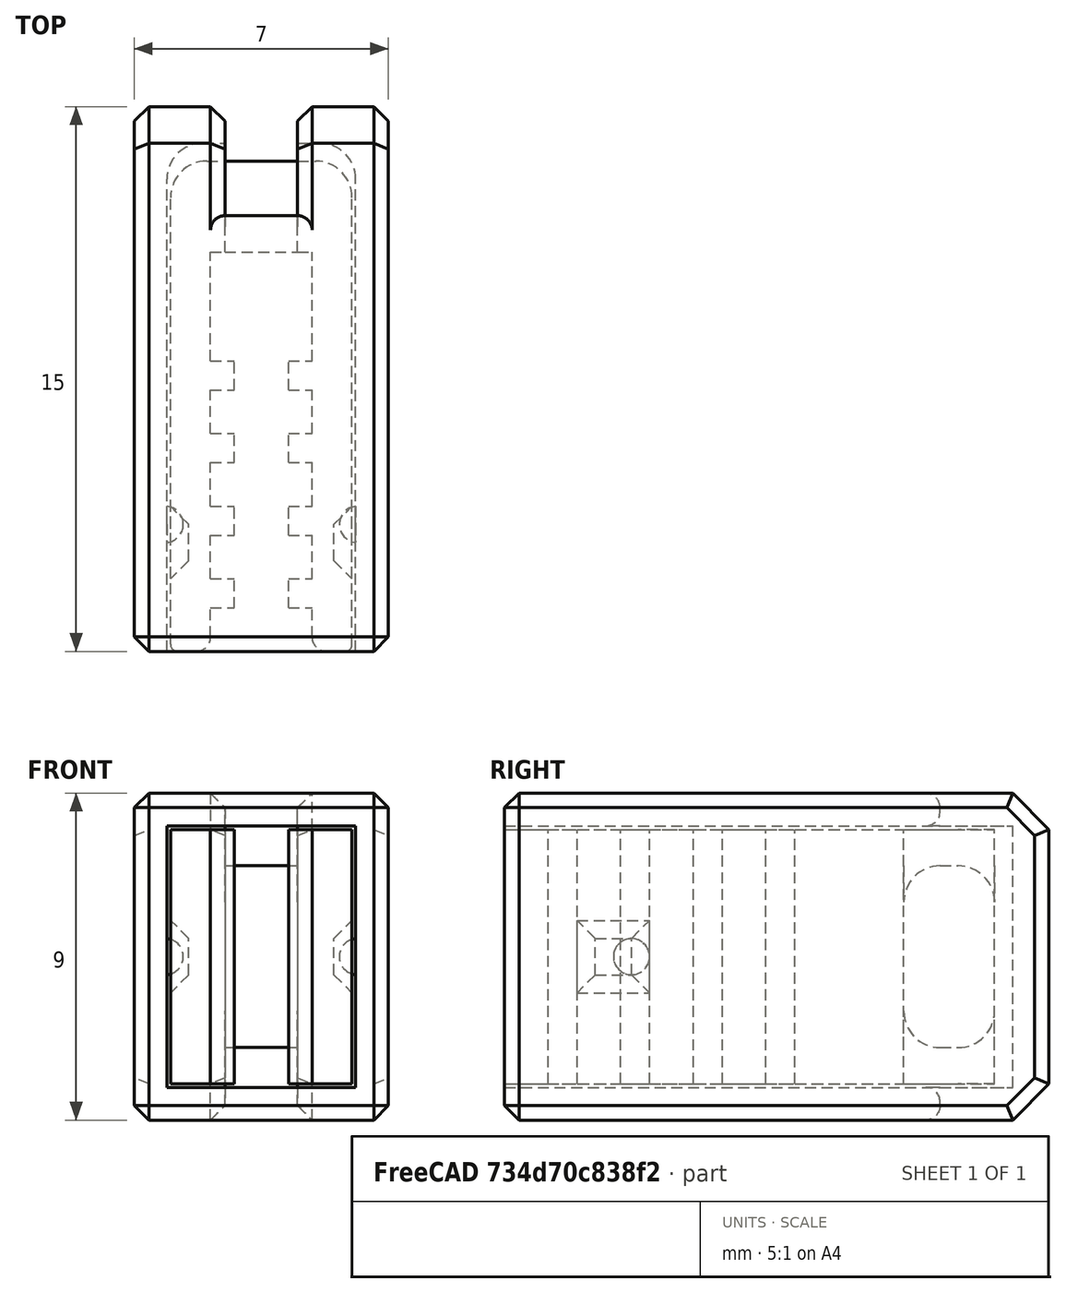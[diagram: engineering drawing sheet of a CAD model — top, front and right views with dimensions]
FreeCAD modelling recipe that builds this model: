
FCSTD DOCUMENT  (FreeCAD 0.19R24291 (Git))
Label: 2gt-strap
License: Other
LicenseURL: GPL3
objects: Part::Box×14, Part::Fillet×6, Part::Cut×5, Part::MultiFuse×4, Part::Chamfer×3, Part::Sphere×2
note: 34 computed .brp shape members not serialized (recipe doc carries the construction recipe); baked Part::Feature solids carry a one-line shape summary decoded from their .brp

FEATURE [Part::Box] Box  label="Cube"
  AttacherType = Attacher::AttachEngine3D
  Height = 7
  Length = 1.5
  Placement = pos=(-0.75,0,0) rot=(0,0,1;0rad)
  Width = 10
FEATURE [Part::Box] Box001  label="Cube001"
  AttacherType = Attacher::AttachEngine3D
  Height = 7
  Length = 2.8
  Placement = pos=(-1.4,0,0) rot=(0,0,1;0rad)
  Width = 1.2
FEATURE [Part::Box] Box002  label="Cube002"
  AttacherType = Attacher::AttachEngine3D
  Height = 7
  Length = 2.8
  Placement = pos=(-1.4,2,0) rot=(0,0,1;0rad)
  Width = 1.2
FEATURE [Part::Box] Box003  label="Cube003"
  AttacherType = Attacher::AttachEngine3D
  Height = 7
  Length = 2.8
  Placement = pos=(-1.4,4,0) rot=(0,0,1;0rad)
  Width = 1.2
FEATURE [Part::Box] Box004  label="Cube004"
  AttacherType = Attacher::AttachEngine3D
  Height = 7
  Length = 2.8
  Placement = pos=(-1.4,6,0) rot=(0,0,1;0rad)
  Width = 1.2
FEATURE [Part::Box] Box005  label="Cube005"
  AttacherType = Attacher::AttachEngine3D
  Height = 7
  Length = 2.8
  Placement = pos=(-1.4,8,0) rot=(0,0,1;0rad)
  Width = 3
FEATURE [Part::Box] Box006  label="Cube006"
  AttacherType = Attacher::AttachEngine3D
  Height = 7
  Length = 5
  Placement = pos=(-2.5,0,0) rot=(0,0,1;0rad)
  Width = 13.5
FEATURE [Part::MultiFuse] Fusion
  Shapes = -> [Box005,Box,Box001,Box002,Box003,Box004]
FEATURE [Part::Box] Box007  label="Cube007"
  AttacherType = Attacher::AttachEngine3D
  Height = 1
  Length = 2
  Placement = pos=(-1,11,0) rot=(0,0,1;0rad)
  Width = 2.5
FEATURE [Part::Box] Box008  label="Cube008"
  AttacherType = Attacher::AttachEngine3D
  Height = 1
  Length = 2
  Placement = pos=(-1,11,6) rot=(0,0,1;0rad)
  Width = 2.5
FEATURE [Part::MultiFuse] Fusion001
  Shapes = -> [Box008,Box007]
FEATURE [Part::Box] Box009  label="Cube009"
  AttacherType = Attacher::AttachEngine3D
  Height = 9
  Length = 7
  Placement = pos=(-3.5,0,-1) rot=(0,0,1;0rad)
  Width = 15
FEATURE [Part::Box] Box010  label="Cube010"
  AttacherType = Attacher::AttachEngine3D
  Height = 7.2
  Length = 5.2
  Placement = pos=(-2.6,0,-0.1) rot=(0,0,1;0rad)
  Width = 14
FEATURE [Part::Box] Box011  label="Cube011"
  AttacherType = Attacher::AttachEngine3D
  Height = 11
  Length = 2
  Placement = pos=(-1,12,-2) rot=(0,0,1;0rad)
  Width = 4
FEATURE [Part::Sphere] Sphere
  Angle1 = -90
  Angle2 = 90
  Angle3 = 360
  AttacherType = Attacher::AttachEngine3D
  Placement = pos=(-2.65,3.5,3.5) rot=(0,0,1;0rad)
  Radius = 0.5
FEATURE [Part::Sphere] Sphere001
  Angle1 = -90
  Angle2 = 90
  Angle3 = 360
  AttacherType = Attacher::AttachEngine3D
  Placement = pos=(2.65,3.5,3.5) rot=(0,0,1;0rad)
  Radius = 0.5
FEATURE [Part::Box] Box012  label="Cube012"
  AttacherType = Attacher::AttachEngine3D
  Height = 2
  Length = 1
  Placement = pos=(2,2,2.5) rot=(0,0,1;0rad)
  Width = 2
FEATURE [Part::Box] Box013  label="Cube013"
  AttacherType = Attacher::AttachEngine3D
  Height = 2
  Length = 1
  Placement = pos=(-3,2,2.5) rot=(0,0,1;0rad)
  Width = 2
FEATURE [Part::Cut] Cut
  Base = -> Box006
  Tool = -> Fusion
FEATURE [Part::MultiFuse] Fusion005
  Shapes = -> [Box012,Box013]
FEATURE [Part::Cut] Cut004
  Base = -> Cut
  Tool = -> Fusion001
FEATURE [Part::Chamfer] Chamfer
  Base = -> Fusion005
  Edges = 8 edges r=0.5: [Edge1,Edge2,Edge3,Edge4,Edge17,Edge18,Edge19,Edge20]
FEATURE [Part::Cut] Cut005
  Base = -> Cut004
  Tool = -> Chamfer
FEATURE [Part::Fillet] Fillet
  Base = -> Cut005
  Edges = 4 edges r=1: [Edge53,Edge59,Edge73,Edge79]
FEATURE [Part::Fillet] Fillet007
  Base = -> Fillet
  Edges = 2 edges r=1: [Edge4,Edge12]
FEATURE [Part::Fillet] Fillet008
  Base = -> Fillet007
  Edges = 2 edges r=0.4: [Edge138,Edge162]
FEATURE [Part::Fillet] Fillet009
  Base = -> Fillet008
  Edges = 2 edges r=0.2: [Edge25,Edge175]
FEATURE [Part::Cut] Cut006
  Base = -> Box009
  Tool = -> Box010
FEATURE [Part::Cut] Cut007
  Base = -> Cut006
  Tool = -> Box011
FEATURE [Part::Fillet] Fillet010
  Base = -> Cut007
  Edges = 2 edges r=1: [Edge33,Edge41]
FEATURE [Part::Fillet] Fillet011
  Base = -> Fillet010
  Edges = 4 edges r=0.4: [Edge9,Edge25,Edge43,Edge44]
FEATURE [Part::Chamfer] Chamfer001
  Base = -> Fillet011
  Edges = 4 edges r=1: [Edge63,Edge66,Edge68,Edge70]
FEATURE [Part::Chamfer] Chamfer002
  Base = -> Chamfer001
  Edges = 24 edges r=0.4: [Edge1,Edge2,Edge3,Edge4,Edge5,Edge19,Edge21,Edge22,Edge23,Edge27,Edge29,Edge33,Edge37,Edge39,Edge40,Edge41,Edge71,Edge72,Edge73,Edge75,Edge77,Edge78,Edge79,Edge80]
FEATURE [Part::MultiFuse] Fusion006
  Shapes = -> [Sphere001,Sphere,Chamfer002]
